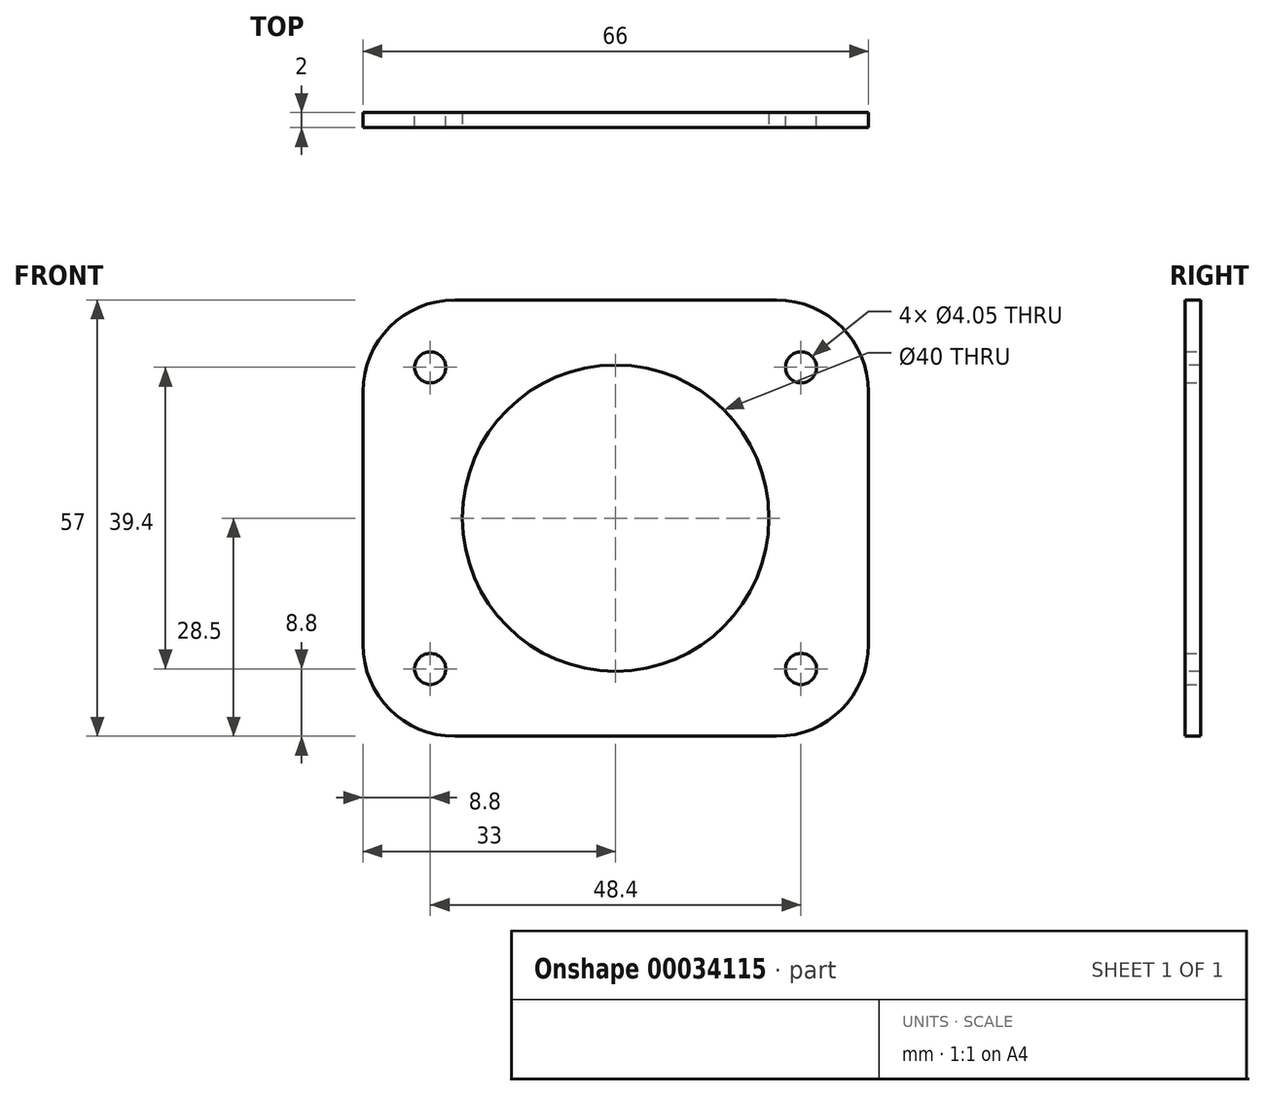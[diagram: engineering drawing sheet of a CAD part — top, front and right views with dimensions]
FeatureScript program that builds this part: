
annotation { "Feature Type Name" : "Feature", "Feature Type Description" : "" }
export const myFeature = defineFeature(function(context is Context, id is Id, definition is map)
    precondition{}
    {
        {
            var Q0;
            Q0=qCreatedBy(makeId("Front.planeOp"),FACE);
            var sketch = newSketch(context, id + "F0", { "sketchPlane" : qUnion([Q0])});
            skLineSegment(sketch, "E0.rect.bottom", {"start": v(21, -28.5) * mm, "end": v(-21, -28.5) * mm});
            skLineSegment(sketch, "E0.rect.top", {"start": v(21, 28.5) * mm, "end": v(-21, 28.5) * mm});
            skLineSegment(sketch, "E0.rect.left", {"start": v(33, -16.5) * mm, "end": v(33, 16.5) * mm});
            skLineSegment(sketch, "E0.rect.right", {"start": v(-33, -16.5) * mm, "end": v(-33, 16.5) * mm});
            skPoint(sketch, "E0.rect.middle", {"position": v(0, 0) * mm});
            skPoint(sketch, "E1.visualSharp", {"position": v(-33, 28.5) * mm});
            skPoint(sketch, "E2.visualSharp", {"position": v(-33, -28.5) * mm});
            skPoint(sketch, "E3.visualSharp", {"position": v(33, -28.5) * mm});
            skPoint(sketch, "E4.visualSharp", {"position": v(33, 28.5) * mm});
            skCircle(sketch, "E5", {"center": v(24.2, 19.7) * mm, "radius": 2.02 * mm});
            skCircle(sketch, "E6", {"center": v(-24.2, 19.7) * mm, "radius": 2.02 * mm});
            skCircle(sketch, "E7", {"center": v(-24.2, -19.7) * mm, "radius": 2.02 * mm});
            skCircle(sketch, "E8", {"center": v(24.2, -19.7) * mm, "radius": 2.02 * mm});
            skArc(sketch, "E9.filletArc", {"start": v(-21, 28.5) * mm, "mid": v(-29.49, 24.99) * mm, "end": v(-33, 16.5) * mm});
            skArc(sketch, "E10.filletArc", {"start": v(33, 16.5) * mm, "mid": v(29.49, 24.99) * mm, "end": v(21, 28.5) * mm});
            skArc(sketch, "E11.filletArc", {"start": v(21, -28.5) * mm, "mid": v(29.49, -24.99) * mm, "end": v(33, -16.5) * mm});
            skArc(sketch, "E12.filletArc", {"start": v(-33, -16.5) * mm, "mid": v(-29.49, -24.99) * mm, "end": v(-21, -28.5) * mm});
            skSolve(sketch);
        }
        {
            var Q0;
            Q0=makeQuery(id+"F0.imprint","IMPRINT",FACE,{"disambiguationData":[TD([[makeQuery(id+"F0.imprint","IMPRINT",EDGE,{"derivedFrom":sQuery(id+"F0.wireOp",EDGE,"E0.rect.bottom")}),-1.0]])]});
            extrude(context, id + "F1", {"entities" : qUnion([Q0]), "depth" : 2 * mm});
        }
        {
            var Q0;
            Q0=makeQuery(id+"F1.opExtrude","CAP_FACE",FACE,{"disambiguationData":[OSD([sQuery(id+"F0.wireOp",EDGE,"E0.rect.bottom"),sQuery(id+"F0.wireOp",EDGE,"E0.rect.top"),sQuery(id+"F0.wireOp",EDGE,"E0.rect.left"),sQuery(id+"F0.wireOp",EDGE,"E0.rect.right"),sQuery(id+"F0.wireOp",EDGE,"E5"),sQuery(id+"F0.wireOp",EDGE,"E6"),sQuery(id+"F0.wireOp",EDGE,"E7"),sQuery(id+"F0.wireOp",EDGE,"E8"),sQuery(id+"F0.wireOp",EDGE,"E9.filletArc"),sQuery(id+"F0.wireOp",EDGE,"E10.filletArc"),sQuery(id+"F0.wireOp",EDGE,"E11.filletArc"),sQuery(id+"F0.wireOp",EDGE,"E12.filletArc")])],"isStart":false});
            var sketch = newSketch(context, id + "F2", { "sketchPlane" : qUnion([Q0])});
            skCircle(sketch, "E13", {"center": v(0, 0) * mm, "radius": 20 * mm});
            skSolve(sketch);
        }
        {
            var Q0;
            Q0=qSketchRegion(id+"F2",true);
            extrude(context, id + "F3", {"entities" : qUnion([Q0]), "operationType" : NewBodyOperationType.REMOVE, "oppositeDirection" : true, "depth" : 25 * mm});
        }
    });
